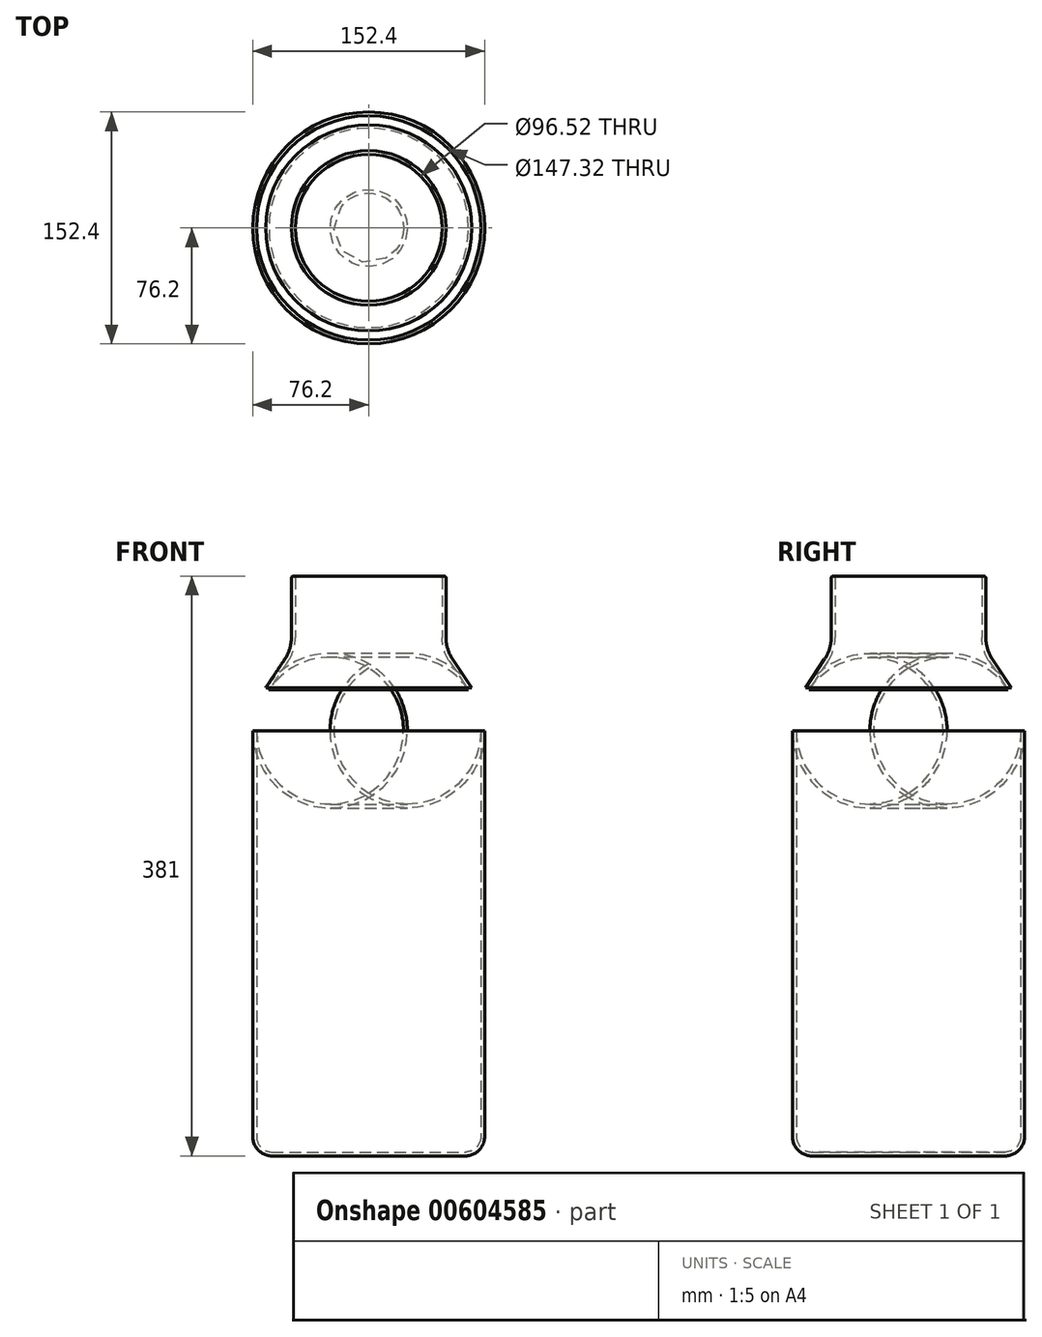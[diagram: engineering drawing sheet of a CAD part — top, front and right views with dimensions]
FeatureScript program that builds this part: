
annotation { "Feature Type Name" : "Feature", "Feature Type Description" : "" }
export const myFeature = defineFeature(function(context is Context, id is Id, definition is map)
    precondition{}
    {
        {
            var Q0;
            Q0=qCreatedBy(makeId("Front.planeOp"),FACE);
            var sketch = newSketch(context, id + "F0", { "sketchPlane" : qUnion([Q0])});
            skLineSegment(sketch, "E0", {"start": v(76.2, 279.4) * mm, "end": v(76.2, 12.7) * mm});
            skLineSegment(sketch, "E1", {"start": v(0, -31.4) * mm, "end": v(0, 429.8) * mm, "construction": true});
            skLineSegment(sketch, "E2", {"start": v(-19.62, 294.78) * mm, "end": v(131.15, 294.78) * mm, "construction": true});
            skLineSegment(sketch, "E3", {"start": v(-19.62, 332.88) * mm, "end": v(121.7, 332.88) * mm, "construction": true});
            skLineSegment(sketch, "E4", {"start": v(50.8, 381) * mm, "end": v(50.8, 340.57) * mm});
            skLineSegment(sketch, "E5", {"start": v(55.07, 326.48) * mm, "end": v(67.67, 307.58) * mm});
            skLineSegment(sketch, "E6", {"start": v(0, 0) * mm, "end": v(63.5, 0) * mm});
            skPoint(sketch, "E7.orphan", {"position": v(76.2, -3.85) * mm});
            skPoint(sketch, "E8.visualSharp", {"position": v(76.2, 294.78) * mm});
            skArc(sketch, "E8.filletArc", {"start": v(76.2, 279.4) * mm, "mid": v(74.02, 294.12) * mm, "end": v(67.67, 307.58) * mm});
            skPoint(sketch, "E9.visualSharp", {"position": v(50.8, 332.88) * mm});
            skArc(sketch, "E9.filletArc", {"start": v(50.8, 340.57) * mm, "mid": v(51.89, 333.21) * mm, "end": v(55.07, 326.48) * mm});
            skPoint(sketch, "E10.visualSharp", {"position": v(76.2, 0) * mm});
            skArc(sketch, "E10.filletArc", {"start": v(63.5, 0) * mm, "mid": v(72.48, 3.72) * mm, "end": v(76.2, 12.7) * mm});
            skLineSegment(sketch, "E11", {"start": v(50.8, 381) * mm, "end": v(-146.44, 381) * mm, "construction": true});
            skLineSegment(sketch, "E12.0", {"start": v(0, 2.54) * mm, "end": v(63.5, 2.54) * mm});
            skArc(sketch, "E12.1", {"start": v(63.5, 2.54) * mm, "mid": v(70.68, 5.52) * mm, "end": v(73.66, 12.7) * mm});
            skLineSegment(sketch, "E12.2", {"start": v(73.66, 279.4) * mm, "end": v(73.66, 12.7) * mm});
            skLineSegment(sketch, "E12.3", {"start": v(48.26, 381) * mm, "end": v(48.26, 340.57) * mm});
            skArc(sketch, "E12.4", {"start": v(48.26, 340.57) * mm, "mid": v(49.46, 332.47) * mm, "end": v(52.95, 325.07) * mm});
            skLineSegment(sketch, "E12.5", {"start": v(52.95, 325.07) * mm, "end": v(65.55, 306.17) * mm});
            skArc(sketch, "E12.6", {"start": v(73.66, 279.4) * mm, "mid": v(71.59, 293.38) * mm, "end": v(65.55, 306.17) * mm});
            skLineSegment(sketch, "E13", {"start": v(48.26, 381) * mm, "end": v(50.8, 381) * mm});
            skLineSegment(sketch, "E14", {"start": v(0, 2.54) * mm, "end": v(0, 0) * mm});
            skSolve(sketch);
        }
        {
            var Q0;
            Q0=makeQuery(id+"F0.imprint","IMPRINT",FACE,{"disambiguationData":[TD([[makeQuery(id+"F0.imprint","IMPRINT",EDGE,{"derivedFrom":sQuery(id+"F0.wireOp",EDGE,"E0")}),-1.0]])]});
            var Q1;
            Q1=sQuery(id+"F0.wireOp",EDGE,"E1");
            revolve(context, id + "F1", {"entities" : qUnion([Q0]), "axis" : qUnion([Q1]), "revolveType" : RevolveType.FULL});
        }
        {
            var Q0;
            Q0=makeQuery(id+"F1.opRevolve","SWEPT_EDGE",EDGE,{"disambiguationData":[OSD([sQuery(id+"F0.wireOp",EDGE,"E4"),sQuery(id+"F0.wireOp",EDGE,"E13")])]});
            var Q1;
            Q1=makeQuery(id+"F1.opRevolve","SWEPT_EDGE",EDGE,{"disambiguationData":[OSD([sQuery(id+"F0.wireOp",EDGE,"E12.3"),sQuery(id+"F0.wireOp",EDGE,"E13")])]});
            fillet(context, id + "F2", {"entities" : qUnion([Q0, Q1]), "radius" : 1.27 * mm, "tangentPropagation" : true, "allowEdgeOverflow" : false});
        }
    });
